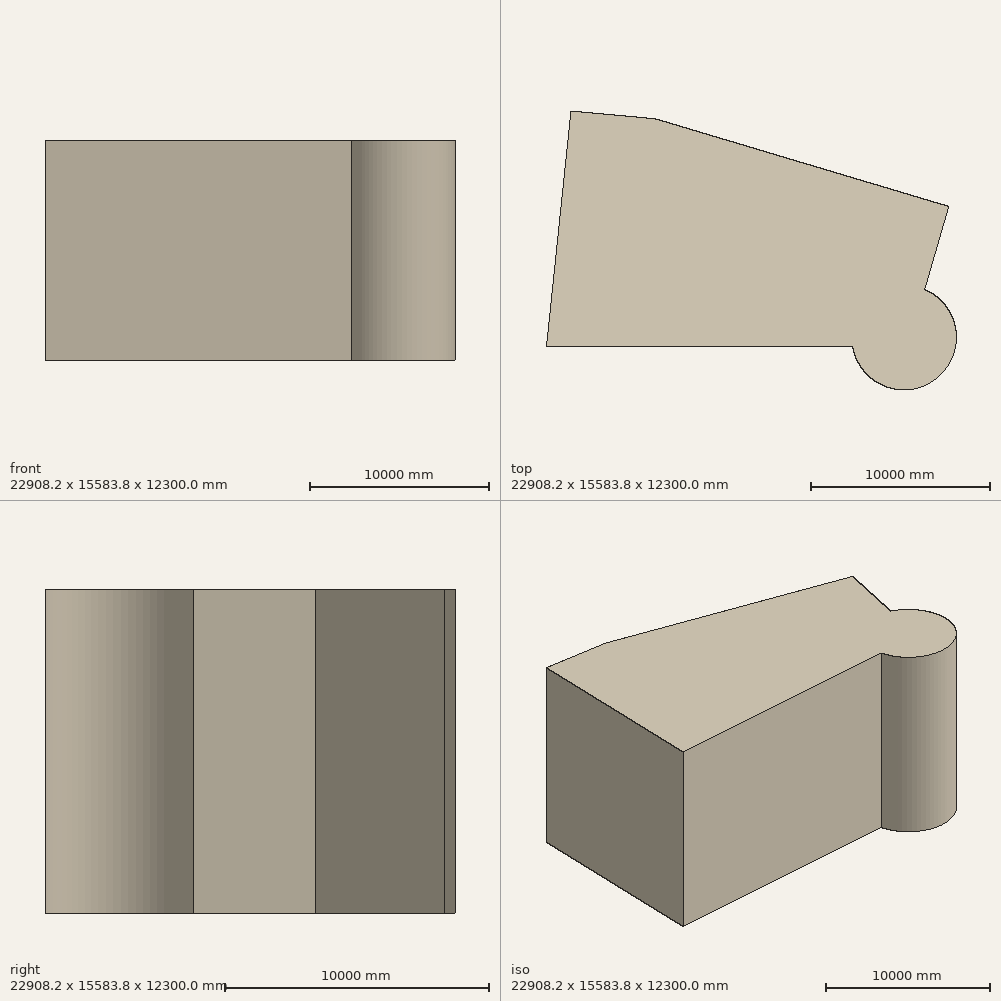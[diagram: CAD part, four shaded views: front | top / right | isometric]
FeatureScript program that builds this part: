
annotation { "Feature Type Name" : "Feature", "Feature Type Description" : "" }
export const myFeature = defineFeature(function(context is Context, id is Id, definition is map)
    precondition{}
    {
        {
            var Q0;
            Q0=qCreatedBy(makeId("Top.planeOp"),FACE);
            cPlane(context, id + "F0", {"entities" : qUnion([Q0]), "cplaneType" : CPlaneType.OFFSET, "offset" : 3800 * mm, "width" : 150 * mm, "height" : 150 * mm});
        }
        {
            var Q0;
            Q0=qCreatedBy(id+"F0.planeOp",FACE);
            cPlane(context, id + "F1", {"entities" : qUnion([Q0]), "cplaneType" : CPlaneType.OFFSET, "offset" : 3300 * mm, "width" : 150 * mm, "height" : 150 * mm});
        }
        {
            var Q0;
            Q0=qCreatedBy(id+"F1.planeOp",FACE);
            cPlane(context, id + "F2", {"entities" : qUnion([Q0]), "cplaneType" : CPlaneType.OFFSET, "offset" : 3160 * mm, "width" : 150 * mm, "height" : 150 * mm});
        }
        {
            var Q0;
            Q0=qCreatedBy(id+"F2.planeOp",FACE);
            cPlane(context, id + "F3", {"entities" : qUnion([Q0]), "cplaneType" : CPlaneType.OFFSET, "offset" : 500 * mm, "width" : 150 * mm, "height" : 150 * mm});
        }
        {
            var Q0;
            Q0=qCreatedBy(id+"F3.planeOp",FACE);
            cPlane(context, id + "F4", {"entities" : qUnion([Q0]), "cplaneType" : CPlaneType.OFFSET, "offset" : 1400 * mm, "oppositeDirection" : true, "width" : 150 * mm, "height" : 150 * mm});
        }
        {
            var Q0;
            Q0=qCreatedBy(makeId("Top.planeOp"),FACE);
            var sketch = newSketch(context, id + "F5", { "sketchPlane" : qUnion([Q0])});
            skLineSegment(sketch, "E0", {"start": v(0, 0) * mm, "end": v(20210, 0) * mm, "construction": true});
            skLineSegment(sketch, "E1", {"start": v(20210, 0) * mm, "end": v(22485.16, 7836.4) * mm, "construction": true});
            skLineSegment(sketch, "E2", {"start": v(22485.16, 7836.4) * mm, "end": v(6071.14, 12737.09) * mm});
            skLineSegment(sketch, "E3", {"start": v(6071.14, 12737.09) * mm, "end": v(1370.92, 13168.83) * mm});
            skLineSegment(sketch, "E4", {"start": v(1370.92, 13168.83) * mm, "end": v(0, 0) * mm});
            skCircle(sketch, "E5", {"center": v(19983.2, 510) * mm, "radius": 2925 * mm, "construction": true});
            skArc(sketch, "E6", {"start": v(17103, 0) * mm, "mid": v(21799.7, -1782.59) * mm, "end": v(21138.27, 3197.27) * mm});
            skLineSegment(sketch, "E7", {"start": v(0, 0) * mm, "end": v(17103, 0) * mm});
            skLineSegment(sketch, "E8", {"start": v(21138.27, 3197.27) * mm, "end": v(22485.16, 7836.4) * mm});
            skSolve(sketch);
        }
        {
            var Q0;
            Q0=makeQuery(id+"F5.imprint","IMPRINT",FACE,{"disambiguationData":[TD([[makeQuery(id+"F5.imprint","IMPRINT",EDGE,{"derivedFrom":sQuery(id+"F5.wireOp",EDGE,"E2")}),1.0]])]});
            extrude(context, id + "F6", {"entities" : qUnion([Q0]), "depth" : 12300 * mm, "offsetDistance" : 25 * mm});
        }
    });
